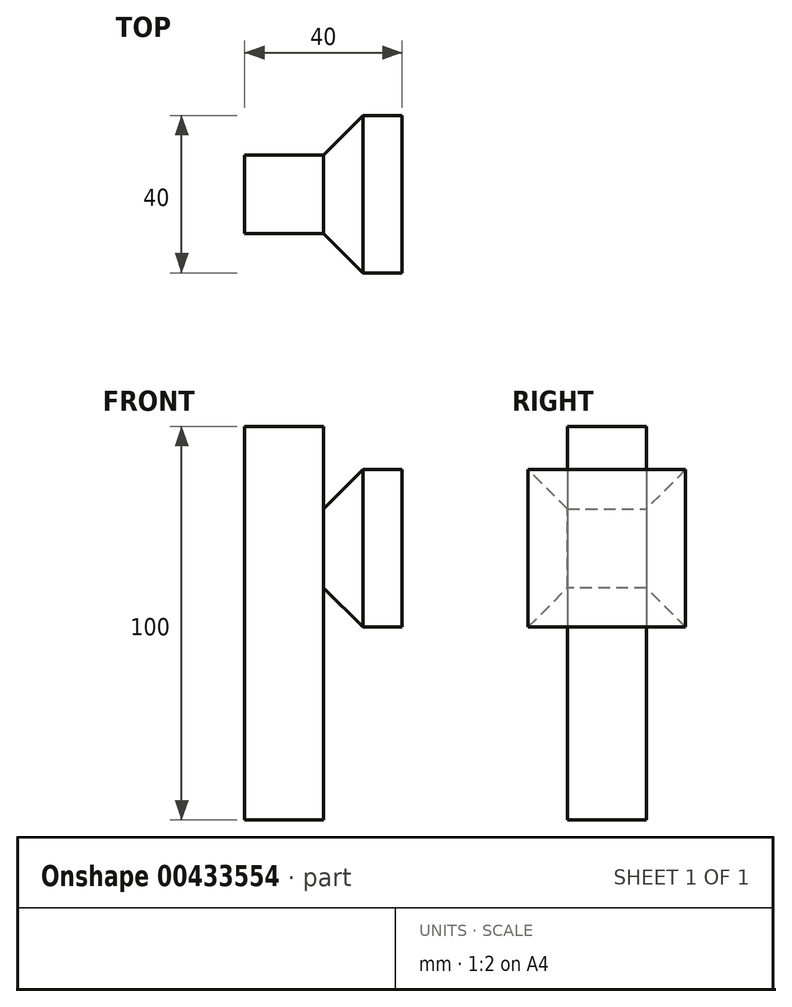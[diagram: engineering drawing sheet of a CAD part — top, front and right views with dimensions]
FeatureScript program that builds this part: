
annotation { "Feature Type Name" : "Feature", "Feature Type Description" : "" }
export const myFeature = defineFeature(function(context is Context, id is Id, definition is map)
    precondition{}
    {
        {
            var Q0;
            Q0=qCreatedBy(makeId("Top.planeOp"),FACE);
            var sketch = newSketch(context, id + "F0", { "sketchPlane" : qUnion([Q0])});
            skLineSegment(sketch, "E0.bottom", {"start": v(10, -10) * mm, "end": v(-10, -10) * mm});
            skLineSegment(sketch, "E0.top", {"start": v(10, 10) * mm, "end": v(-10, 10) * mm});
            skLineSegment(sketch, "E0.left", {"start": v(10, -10) * mm, "end": v(10, 10) * mm});
            skLineSegment(sketch, "E0.right", {"start": v(-10, -10) * mm, "end": v(-10, 10) * mm});
            skPoint(sketch, "E0.middle", {"position": v(0, 0) * mm});
            skSolve(sketch);
        }
        {
            var Q0;
            Q0=makeQuery(id+"F0.imprint","IMPRINT",FACE,{"disambiguationData":[TD([[makeQuery(id+"F0.imprint","IMPRINT",EDGE,{"derivedFrom":sQuery(id+"F0.wireOp",EDGE,"E0.bottom")}),-1.0]])]});
            extrude(context, id + "F1", {"entities" : qUnion([Q0]), "depth" : 100 * mm});
        }
        {
            var Q0;
            Q0=makeQuery(id+"F1.opExtrude","SWEPT_FACE",FACE,{"disambiguationData":[OSD([sQuery(id+"F0.wireOp",EDGE,"E0.left")])]});
            var sketch = newSketch(context, id + "F2", { "sketchPlane" : qUnion([Q0])});
            skLineSegment(sketch, "E1.bottom", {"start": v(20, 89.02) * mm, "end": v(-20, 89.02) * mm});
            skLineSegment(sketch, "E1.top", {"start": v(20, 49.02) * mm, "end": v(-20, 49.02) * mm});
            skLineSegment(sketch, "E1.left", {"start": v(20, 89.02) * mm, "end": v(20, 49.02) * mm});
            skLineSegment(sketch, "E1.right", {"start": v(-20, 89.02) * mm, "end": v(-20, 49.02) * mm});
            skPoint(sketch, "E1.middle", {"position": v(0, 69.02) * mm});
            skSolve(sketch);
        }
        {
            var Q0;
            {var subQ0=sQuery(id+"F2.wireOp",EDGE,"E1.right");Q0=makeQuery(id+"F2.imprint","IMPRINT",FACE,{"disambiguationData":[TD([[makeQuery(id+"F2.imprint","IMPRINT",EDGE,{"derivedFrom":subQ0}),1.0]])]});}
            var Q1;
            {var subQ0=sQuery(id+"F2.wireOp",EDGE,"E1.bottom");var subQ1=sQuery(id+"F0.wireOp",EDGE,"E0.left");var subQ2=makeQuery(id+"F1.opExtrude","SWEPT_EDGE",EDGE,{"disambiguationData":[OSD([sQuery(id+"F0.wireOp",EDGE,"E0.top"),subQ1])]});var subQ3=makeQuery(id+"F2.imprint","INTERSECT",VERTEX,{"derivedFrom":[subQ2,subQ0]});Q1=makeQuery(id+"F2.imprint","IMPRINT",FACE,{"disambiguationData":[TD([[makeQuery(id+"F2.imprint","IMPRINT",EDGE,{"disambiguationData":[TD([[subQ3,-1.0]])],"derivedFrom":subQ0}),1.0]])]});}
            var Q2;
            {var subQ0=sQuery(id+"F2.wireOp",EDGE,"E1.left");Q2=makeQuery(id+"F2.imprint","IMPRINT",FACE,{"disambiguationData":[TD([[makeQuery(id+"F2.imprint","IMPRINT",EDGE,{"derivedFrom":subQ0}),-1.0]])]});}
            extrude(context, id + "F3", {"entities" : qUnion([Q0, Q1, Q2]), "depth" : 20 * mm});
        }
        {
            var Q0;
            Q0=makeQuery(id+"F3.opExtrude","CAP_EDGE",EDGE,{"disambiguationData":[OSD([sQuery(id+"F2.wireOp",EDGE,"E1.bottom")])],"isStart":true});
            var Q1;
            Q1=makeQuery(id+"F3.opExtrude","CAP_EDGE",EDGE,{"disambiguationData":[OSD([sQuery(id+"F2.wireOp",EDGE,"E1.right")])],"isStart":true});
            var Q2;
            Q2=makeQuery(id+"F3.opExtrude","CAP_EDGE",EDGE,{"disambiguationData":[OSD([sQuery(id+"F2.wireOp",EDGE,"E1.top")])],"isStart":true});
            var Q3;
            Q3=makeQuery(id+"F3.opExtrude","CAP_EDGE",EDGE,{"disambiguationData":[OSD([sQuery(id+"F2.wireOp",EDGE,"E1.left")])],"isStart":true});
            chamfer(context, id + "F4", {"entities" : qUnion([Q0, Q1, Q2, Q3]), "width" : 10 * mm, "tangentPropagation" : true});
        }
    });
